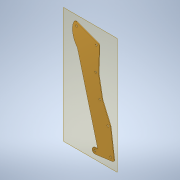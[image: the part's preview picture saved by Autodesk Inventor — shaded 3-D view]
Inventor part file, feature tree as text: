
AUTODESK INVENTOR PART (.ipt)
format: ipt  version: 2020 (Build 240168000, 168)  size: 147,968 bytes
history: native  units: mm
features: reference x6, other x5, plane x1, extrude x1, sketch x1
ambient origin geometry x8: Origin, YZ Plane, XZ Plane, XY Plane, X Axis, Y Axis, Z Axis, Center Point
bodies: Solid1 (feature_tree)
feature tree (14):
  plane  "Work Plane1"
  extrude  "Extrusion1"  [1 undecoded]
  sketch  "Sketch1"  dims[d0=1.0mm d1=0.0mm]
  reference  "Reference1"
  reference  "Reference2"
  reference  "Reference3"
  reference  "Reference4"
  reference  "Reference5"
  reference  "Reference6"
  other  "Kauri Assembly.iam"
  other  "Kauri side plate:2"
  other  "Kauri mid plate v2:1"
  other  "Kauri arm disc aero:1"
  other  "Kauri arm long disc aero:2"
note: 1 required parameter value undecoded (feature->parameter linkage not recoverable at this tier; creation-order binding heuristic only, values carry confidence <= 0.55)
